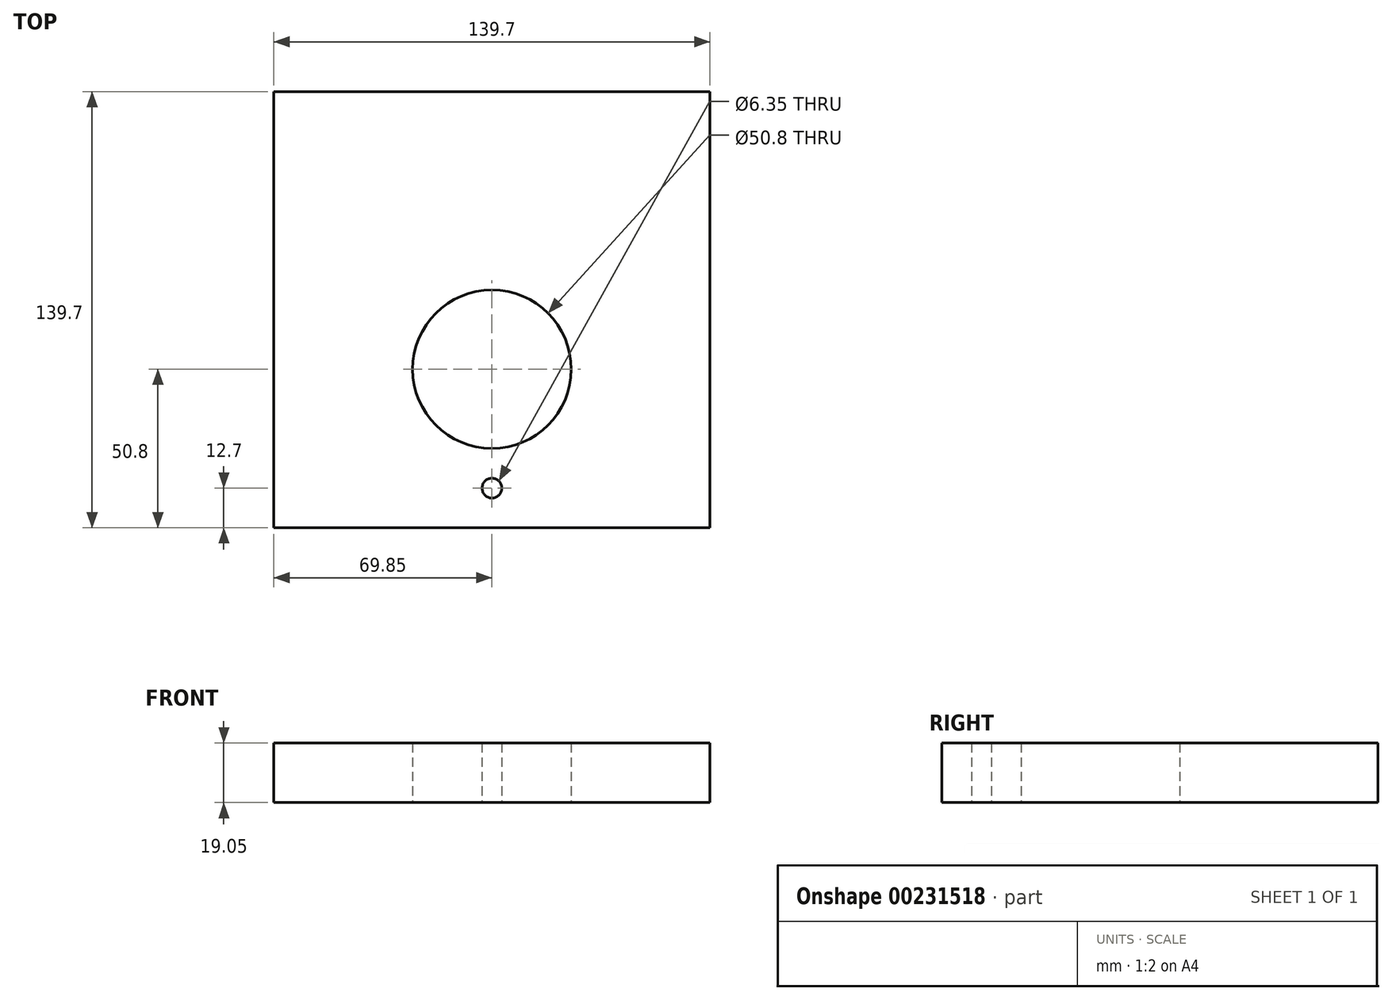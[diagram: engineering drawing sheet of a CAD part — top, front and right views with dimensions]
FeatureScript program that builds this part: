
annotation { "Feature Type Name" : "Feature", "Feature Type Description" : "" }
export const myFeature = defineFeature(function(context is Context, id is Id, definition is map)
    precondition{}
    {
        {
            var Q0;
            Q0=qCreatedBy(makeId("Top.planeOp"),FACE);
            var sketch = newSketch(context, id + "F0", { "sketchPlane" : qUnion([Q0])});
            skLineSegment(sketch, "E0.bottom", {"start": v(69.85, -69.85) * mm, "end": v(-69.85, -69.85) * mm});
            skLineSegment(sketch, "E0.top", {"start": v(69.85, 69.85) * mm, "end": v(-69.85, 69.85) * mm});
            skLineSegment(sketch, "E0.left", {"start": v(69.85, -69.85) * mm, "end": v(69.85, 69.85) * mm});
            skLineSegment(sketch, "E0.right", {"start": v(-69.85, -69.85) * mm, "end": v(-69.85, 69.85) * mm});
            skPoint(sketch, "E0.middle", {"position": v(0, 0) * mm});
            skLineSegment(sketch, "E1", {"start": v(0, -69.85) * mm, "end": v(0, -57.15) * mm});
            skLineSegment(sketch, "E2", {"start": v(0, -57.15) * mm, "end": v(0, -19.05) * mm});
            skCircle(sketch, "E3", {"center": v(0, -57.15) * mm, "radius": 3.18 * mm});
            skCircle(sketch, "E4", {"center": v(0, -19.05) * mm, "radius": 25.4 * mm});
            skSolve(sketch);
        }
        {
            var Q0;
            Q0 = qSketchRegion(id + "F0", true);
            extrude(context, id + "F1", {"entities" : qUnion([Q0]), "depth" : 19.05 * mm});
        }
    });
